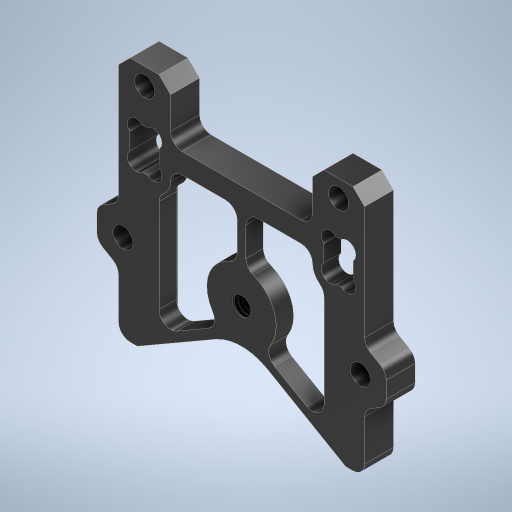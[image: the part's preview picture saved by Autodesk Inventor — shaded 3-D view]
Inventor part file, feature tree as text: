
AUTODESK INVENTOR PART (.ipt)
format: ipt  version: 2024.2 (Build 282272000, 272)  size: 522,240 bytes
history: native  units: mm
features: extrude x2, sketch x1, hole x1
ambient origin geometry x8: Origin, YZ Plane, XZ Plane, XY Plane, X Axis, Y Axis, Z Axis, Center Point
bodies: Solid1 (feature_tree)
feature tree (4):
  sketch  "Sketch1"  dims[d0=32.0mm d1=43.0mm d2=27.0mm d4=16.0mm d5=15.0mm d12=8.5mm d13=9.5mm d21=5.0mm d22=0.0mm d48=3.242mm d49=8.0mm d50=4.0mm d51=2.0mm d52=90.0deg d53=8.0mm d54=20.594885mm d57=2.0mm d58=0.0mm d72=12.0mm d73=2.0mm d75=27.5mm d79=6.5mm d83=2.0mm d84=1.5mm d86=6.0mm d89=5.0mm d90=5.5mm d91=0.05mm d92=60.0mm d94=360.0deg d96=3.5mm d97=6.0mm d98=6.1mm d99=3.5mm d100=90.0deg d101=8.0mm d102=20.594885mm d104=3.0mm d107=2.0mm d108=2.0mm d109=45.0deg d110=60.0deg d111=0.05mm d112=0.05mm d113=9.0mm d114=6.5mm d115=28.5mm d116=2.0mm d117=5.0mm d118=0.05mm d120=1.5mm d121=1.5mm d124=1.5mm d126=1.5mm d127=1.5mm d129=1.5mm d130=1.5mm d131=1.5mm d132=1.5mm d134=1.5mm d135=27.0mm]
  extrude  "Extrusion1"  Depth=1.5mm
  extrude  "Extrusion2"  Depth=1.5mm
  hole  "Phi3.5"  [1 undecoded]
note: 1 required parameter value undecoded (feature->parameter linkage not recoverable at this tier; creation-order binding heuristic only, values carry confidence <= 0.55)
